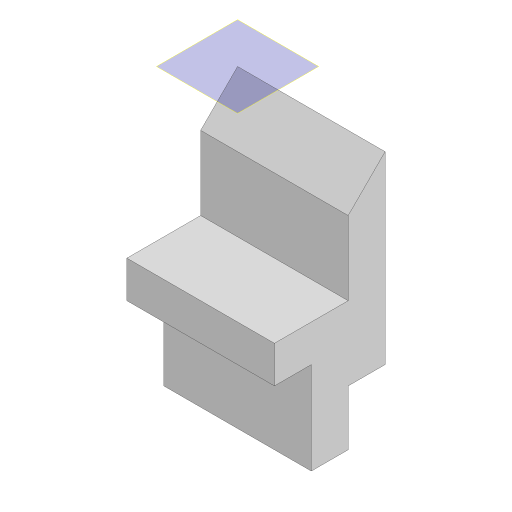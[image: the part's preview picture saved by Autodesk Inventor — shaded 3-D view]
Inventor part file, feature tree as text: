
AUTODESK INVENTOR PART (.ipt)
format: ipt  version: 2024.3 (Build 283343000, 343)  size: 98,304 bytes
history: native  units: mm
features: extrude x1, plane x1, sketch x1
ambient origin geometry x8: Origin, YZ Plane, XZ Plane, XY Plane, X Axis, Y Axis, Z Axis, Center Point
bodies: Solid1 (feature_tree)
feature tree (3):
  extrude  "Extrusion1"  Depth=15.0mm
  plane  "Work Plane1"
  sketch  "Sketch1"  dims[d0=65.0mm d1=15.0mm d2=10.0mm d3=10.0mm d4=10.0mm d5=25.0mm d6=10.0mm d7=20.0mm d8=40.0mm d9=0.0mm]
